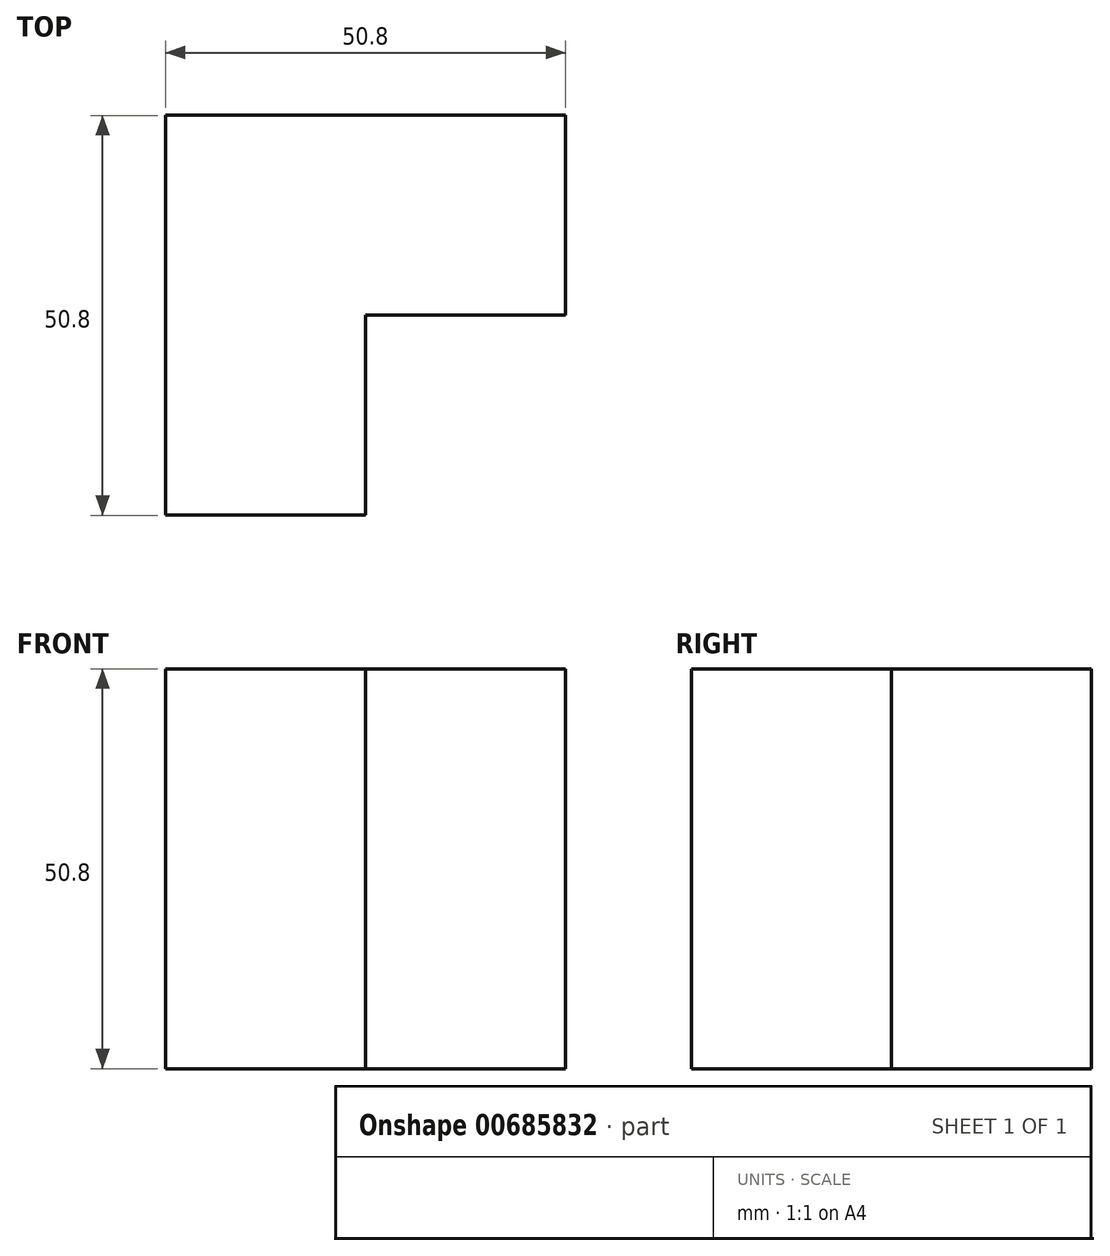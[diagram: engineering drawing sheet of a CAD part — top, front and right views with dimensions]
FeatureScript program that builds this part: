
annotation { "Feature Type Name" : "Feature", "Feature Type Description" : "" }
export const myFeature = defineFeature(function(context is Context, id is Id, definition is map)
    precondition{}
    {
        {
            var Q0;
            Q0=qCreatedBy(makeId("Top.planeOp"),FACE);
            var sketch = newSketch(context, id + "F0", { "sketchPlane" : qUnion([Q0])});
            skLineSegment(sketch, "E0.bottom", {"start": v(-7.05, -29.89) * mm, "end": v(-32.45, -29.89) * mm});
            skLineSegment(sketch, "E0.top", {"start": v(18.35, 20.91) * mm, "end": v(-32.45, 20.91) * mm});
            skLineSegment(sketch, "E0.left", {"start": v(18.35, -4.49) * mm, "end": v(18.35, 20.91) * mm});
            skLineSegment(sketch, "E0.right", {"start": v(-32.45, -29.89) * mm, "end": v(-32.45, 20.91) * mm});
            skLineSegment(sketch, "E1.top", {"start": v(18.35, -4.49) * mm, "end": v(-7.05, -4.49) * mm});
            skLineSegment(sketch, "E1.right", {"start": v(-7.05, -29.89) * mm, "end": v(-7.05, -4.49) * mm});
            skSolve(sketch);
        }
        {
            var Q0;
            Q0 = qSketchRegion(id + "F0", true);
            extrude(context, id + "F1", {"entities" : qUnion([Q0]), "depth" : 50.8 * mm, "offsetDistance" : 25.4 * mm});
        }
    });
